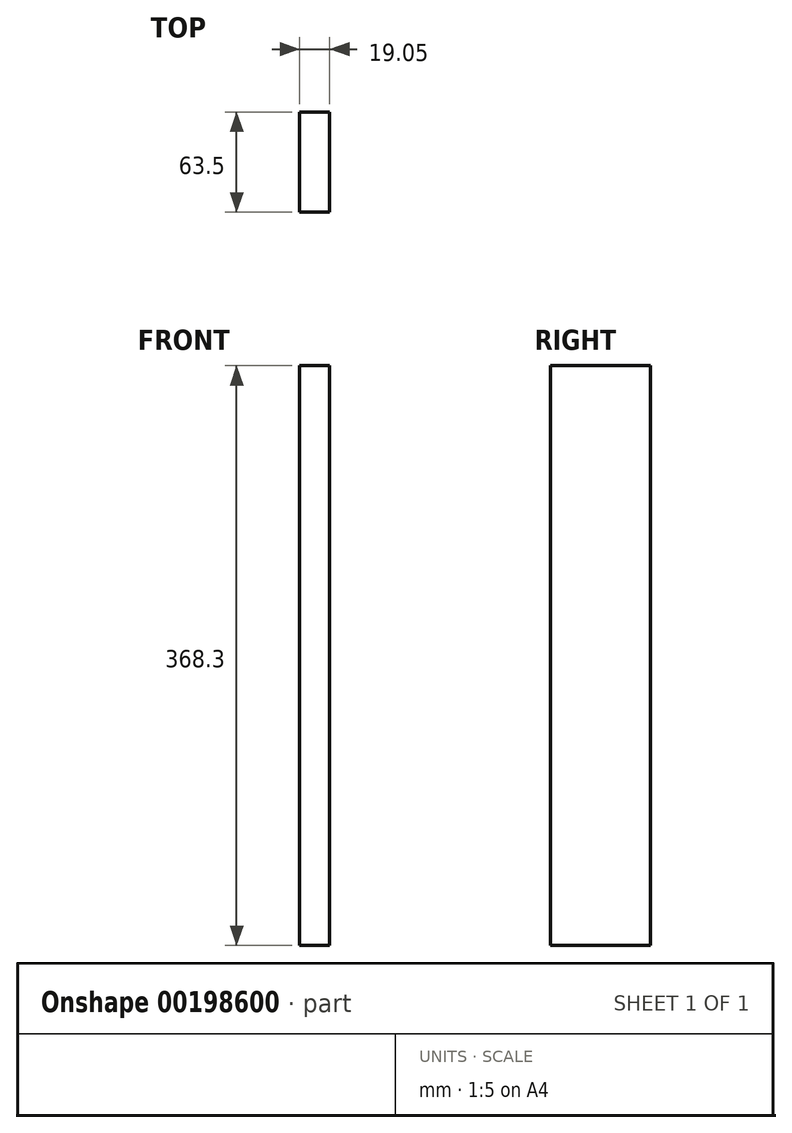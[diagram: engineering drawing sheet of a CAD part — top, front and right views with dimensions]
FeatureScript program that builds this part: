
annotation { "Feature Type Name" : "Feature", "Feature Type Description" : "" }
export const myFeature = defineFeature(function(context is Context, id is Id, definition is map)
    precondition{}
    {
        {
            var Q0;
            Q0=qCreatedBy(makeId("Top.planeOp"),FACE);
            var sketch = newSketch(context, id + "F0", { "sketchPlane" : qUnion([Q0])});
            skLineSegment(sketch, "E0.bottom", {"start": v(0, 0) * mm, "end": v(19.05, 0) * mm});
            skLineSegment(sketch, "E0.top", {"start": v(0, 63.5) * mm, "end": v(19.05, 63.5) * mm});
            skLineSegment(sketch, "E0.left", {"start": v(0, 0) * mm, "end": v(0, 63.5) * mm});
            skLineSegment(sketch, "E0.right", {"start": v(19.05, 0) * mm, "end": v(19.05, 63.5) * mm});
            skSolve(sketch);
        }
        {
            var Q0;
            Q0 = qSketchRegion(id + "F0", true);
            extrude(context, id + "F1", {"entities" : qUnion([Q0]), "depth" : 368.3 * mm});
        }
    });
